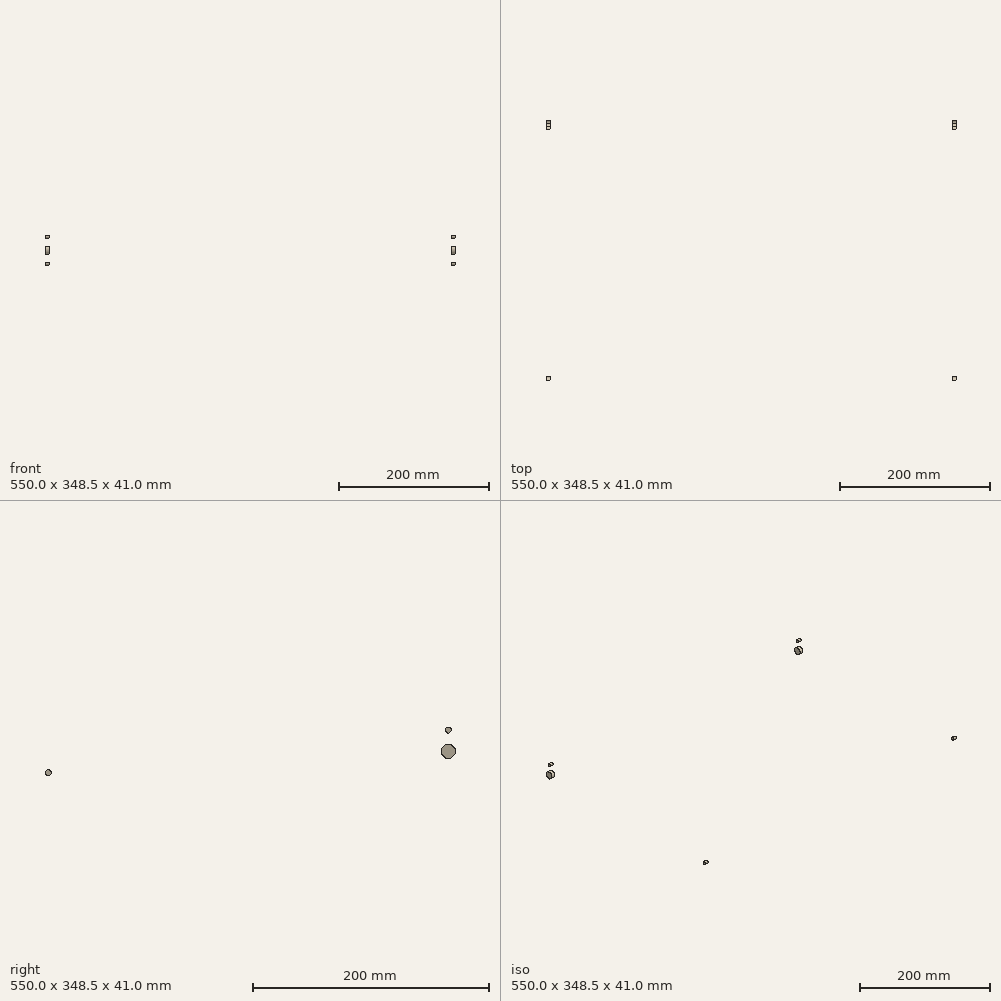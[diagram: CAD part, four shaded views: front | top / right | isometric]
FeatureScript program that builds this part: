
annotation { "Feature Type Name" : "Feature", "Feature Type Description" : "" }
export const myFeature = defineFeature(function(context is Context, id is Id, definition is map)
    precondition{}
    {
        {
            var Q0;
            Q0=qCreatedBy(makeId("Top.planeOp"),FACE);
            var sketch = newSketch(context, id + "F0", { "sketchPlane" : qUnion([Q0])});
            skLineSegment(sketch, "E0.bottom", {"start": v(275, 200) * mm, "end": v(-275, 200) * mm});
            skLineSegment(sketch, "E0.top", {"start": v(275, -200) * mm, "end": v(-275, -200) * mm});
            skLineSegment(sketch, "E0.left", {"start": v(275, 200) * mm, "end": v(275, -200) * mm});
            skLineSegment(sketch, "E0.right", {"start": v(-275, 200) * mm, "end": v(-275, -200) * mm});
            skPoint(sketch, "E0.middle", {"position": v(0, 0) * mm});
            skSolve(sketch);
        }
        {
            var Q0;
            Q0 = qSketchRegion(id + "F0", true);
            var Q1;
            Q1=makeQuery(id+"F0.imprint","IMPRINT",FACE,{"disambiguationData":[TD([[makeQuery(id+"F0.imprint","IMPRINT",EDGE,{"derivedFrom":sQuery(id+"F0.wireOp",EDGE,"E0.bottom")}),1.0]])]});
            extrude(context, id + "F1", {"entities" : qUnion([Q0, Q1]), "depth" : 100 * mm});
        }
        {
            var Q0;
            Q0=makeQuery(id+"F1.opExtrude","CAP_FACE",FACE,{"disambiguationData":[OSD([sQuery(id+"F0.wireOp",EDGE,"E0.bottom"),sQuery(id+"F0.wireOp",EDGE,"E0.top"),sQuery(id+"F0.wireOp",EDGE,"E0.left"),sQuery(id+"F0.wireOp",EDGE,"E0.right")])],"isStart":false});
            shell(context, id + "F2", {"entities" : qUnion([Q0]), "thickness" : 6 * mm});
        }
        {
            var Q0;
            Q0=makeQuery(id+"F1.opExtrude","SWEPT_FACE",FACE,{"disambiguationData":[OSD([sQuery(id+"F0.wireOp",EDGE,"E0.left")])]});
            var sketch = newSketch(context, id + "F3", { "sketchPlane" : qUnion([Q0])});
            skPoint(sketch, "E1", {"position": v(-170, 56) * mm});
            skLineSegment(sketch, "E2", {"start": v(0, 0) * mm, "end": v(0, 100) * mm, "construction": true});
            skPoint(sketch, "E3.MirrorP", {"position": v(170, 56) * mm});
            skCircle(sketch, "E4", {"center": v(-170, 56) * mm, "radius": 6 * mm});
            skCircle(sketch, "E5.MirrorC", {"center": v(170, 56) * mm, "radius": 6 * mm});
            skCircle(sketch, "E6", {"center": v(-170, 74) * mm, "radius": 2.5 * mm});
            skLineSegment(sketch, "E7", {"start": v(-170, 56) * mm, "end": v(-154.18, 56) * mm, "construction": true});
            skCircle(sketch, "E8.MirrorC", {"center": v(-170, 38) * mm, "radius": 2.5 * mm});
            skCircle(sketch, "E9.MirrorC", {"center": v(170, 74) * mm, "radius": 2.5 * mm});
            skCircle(sketch, "E10.MirrorC", {"center": v(170, 38) * mm, "radius": 2.5 * mm});
            skSolve(sketch);
        }
        {
            var Q0;
            Q0=makeQuery(id+"F3.imprint","IMPRINT",FACE,{"disambiguationData":[TD([[makeQuery(id+"F3.imprint","IMPRINT",EDGE,{"derivedFrom":sQuery(id+"F3.wireOp",EDGE,"E6")}),1.0]])]});
            var Q1;
            Q1=makeQuery(id+"F3.imprint","IMPRINT",FACE,{"disambiguationData":[TD([[makeQuery(id+"F3.imprint","IMPRINT",EDGE,{"derivedFrom":sQuery(id+"F3.wireOp",EDGE,"E8.MirrorC")}),-1.0]])]});
            var Q2;
            Q2=makeQuery(id+"F3.imprint","IMPRINT",FACE,{"disambiguationData":[TD([[makeQuery(id+"F3.imprint","IMPRINT",EDGE,{"derivedFrom":sQuery(id+"F3.wireOp",EDGE,"E10.MirrorC")}),1.0]])]});
            var Q3;
            Q3=makeQuery(id+"F3.imprint","IMPRINT",FACE,{"disambiguationData":[TD([[makeQuery(id+"F3.imprint","IMPRINT",EDGE,{"derivedFrom":sQuery(id+"F3.wireOp",EDGE,"E9.MirrorC")}),-1.0]])]});
            var Q4;
            Q4=makeQuery(id+"F3.imprint","IMPRINT",FACE,{"disambiguationData":[TD([[makeQuery(id+"F3.imprint","IMPRINT",EDGE,{"derivedFrom":sQuery(id+"F3.wireOp",EDGE,"E4")}),1.0]])]});
            var Q5;
            Q5=makeQuery(id+"F3.imprint","IMPRINT",FACE,{"disambiguationData":[TD([[makeQuery(id+"F3.imprint","IMPRINT",EDGE,{"derivedFrom":sQuery(id+"F3.wireOp",EDGE,"E5.MirrorC")}),-1.0]])]});
            extrude(context, id + "F4", {"entities" : qUnion([Q0, Q1, Q2, Q3, Q4, Q5]), "operationType" : NewBodyOperationType.REMOVE, "endBound" : BoundingType.THROUGH_ALL, "oppositeDirection" : true, "depth" : 25 * mm});
        }
    });
